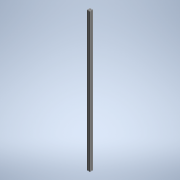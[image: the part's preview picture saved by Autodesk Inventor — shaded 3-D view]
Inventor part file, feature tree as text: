
AUTODESK INVENTOR PART (.ipt)
format: ipt  version: 2022 (Build 260153000, 153)  size: 223,232 bytes
history: native  units: mm (DEFAULTED — no unit token found)
features: other x21, sketch x2, extrude x1, hole x1
ambient origin geometry x8: Origin, YZ Plane, XZ Plane, XY Plane, X Axis, Y Axis, Z Axis, Center Point
bodies: Solid1 (feature_tree)
feature tree (25):
  extrude  "Extrusion1"  TaperAngle=0.0deg  [1 undecoded]
  hole  "Hole1"  [1 undecoded]
  other  "C1_XY"
  other  "C1_YZ"
  other  "C1_ZX"
  other  "C1_X"
  other  "C1_Y"
  other  "C1_Z"
  other  "C1_Center"
  other  "to_frame_cap1_XY"
  other  "to_frame_cap1_YZ"
  other  "to_frame_cap1_ZX"
  other  "to_frame_cap1_X"
  other  "to_frame_cap1_Y"
  other  "to_frame_cap1_Z"
  other  "to_frame_cap1_Center"
  other  "to_frame_cap2_XY"
  other  "to_frame_cap2_YZ"
  other  "to_frame_cap2_ZX"
  other  "to_frame_cap2_X"
  other  "to_frame_cap2_Y"
  other  "to_frame_cap2_Z"
  other  "to_frame_cap2_Center"
  sketch  "Sketch_60"  dims[d2=10.5mm d3=6.0mm d4=4.0mm d5=2.0mm d6=90.0deg d7=1000.0mm d8=0.0mm d9=0.0mm d10=0.0mm d11=0.0mm d12=152.4mm d13=0.872665mm d14=152.4mm d15=0.872665mm]
  sketch  "Sketch2"  dims[d0=2667.0mm d1=0.0mm]
note: 2 required parameter values undecoded (feature->parameter linkage not recoverable at this tier; creation-order binding heuristic only, values carry confidence <= 0.55)
